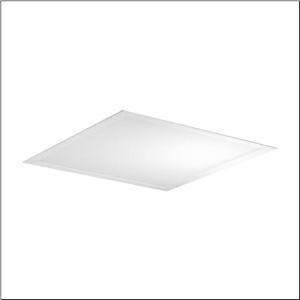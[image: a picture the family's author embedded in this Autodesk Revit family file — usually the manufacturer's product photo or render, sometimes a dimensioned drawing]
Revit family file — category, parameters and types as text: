
# Revit family: apollon_r__31_square_51mp11w72442_ea88
name_source: partatom
category: Lighting Fixtures
units: mm (PartAtom-declared; Revit-internal decimal feet)

## family parameters
Cut with Voids When Loaded = No
Host = Face
Light Source = No
Part Type = Normal
Room Calculation Point = No
Round Connector Dimension = Use Diameter
Shared = No

## types (1)
- Apollon® 31 square (1 x LED, 4000 lm, 27.5 W, 4000K)
    Apparent Load = 28 VA
    CIE Flux Codes = 61 87 97 100 100
    Color Rendering = 80
    Color Temperature = 4000K
    Default Elevation = 1800 mm
    Description = Apollon® 31 square, office luminaire, primary optical cover: micro prismatic cover, of PMMA, CAT 2 (L<= 3000cd/m²), light emission: direct distribution, primary light characteristic: symmetric, installation type: lay-in mounting, LED, rated luminous flux: 4.000lm, luminous efficacy: 145lm/W, light colour: 840, colour temperature: 4000K, with terminal, 3-pole, mains connection: 220..240V, AC, 50/60Hz, rated input power: 28W, housing, of aluminium, traffic white (RAL 9016), module: M625, length: 620mm, width: 620mm, height: 32mm, housing upper side, of sheet steel, galvanised, protection rating (complete): IP20, protection rating (on room side): IP40, insulation class (complete): insulation class II (safety insulation), certification: CE, ENEC, impact resistance: IK03, permissible operating ambient temperature: -20..+40°C, permissible storage temperature: -20..+60°C, packaging unit: 1 piece
    Height = 0 mm  [stored 0 ft]
    Lamp = 1 x LED
    Lamp Light Flux = 4000 lm
    Lamp Power = 27.5 W
    Lamp count = 1
    Length = 620 mm
    Luminous efficacy = 145 lm/W
    Manufacturer = Siteco
    ModVariant = No
    Model = 51MP11W72442
    Mounting Place = Ceiling
    Mounting Type = Recessed
    Number of Poles = 1
    OnlyDefault = Yes
    Power Factor = 1
    Product Name = Apollon® 31 square
    Product group = office luminaire | ceiling recessed
    ProductGroupID = 401
    Protection Class = Protection class II
    Protection Degree = IP 20
    RLX_Detail_Level = 1
    RLX_Emergency_Light_Flux = 0 lm
    RLX_Emergency_Type = 0
    RLX_Emergency_Type_DB = No
    RlxData = <blob elided: 12941 chars, md5=07a08501>
    Socket = socket
    Standby Power = 0 W
    System Light Flux = 4000 lm
    System Power = 28 W
    Type Comments = Product without accessories
    Type Image = l_1291039.jpg
    URL = http://relux.com
    VarID = ---
    Voltage = 0 V
    Weight = 0.00 kg
    Width = 620 mm

note: [stored X ft] marks values corroborated as IEEE doubles in the binary element streams (Revit-internal decimal feet)

## geometry (parser evidence)
native form markers: Sweep x10
no freeform markers — native parametric forms only
